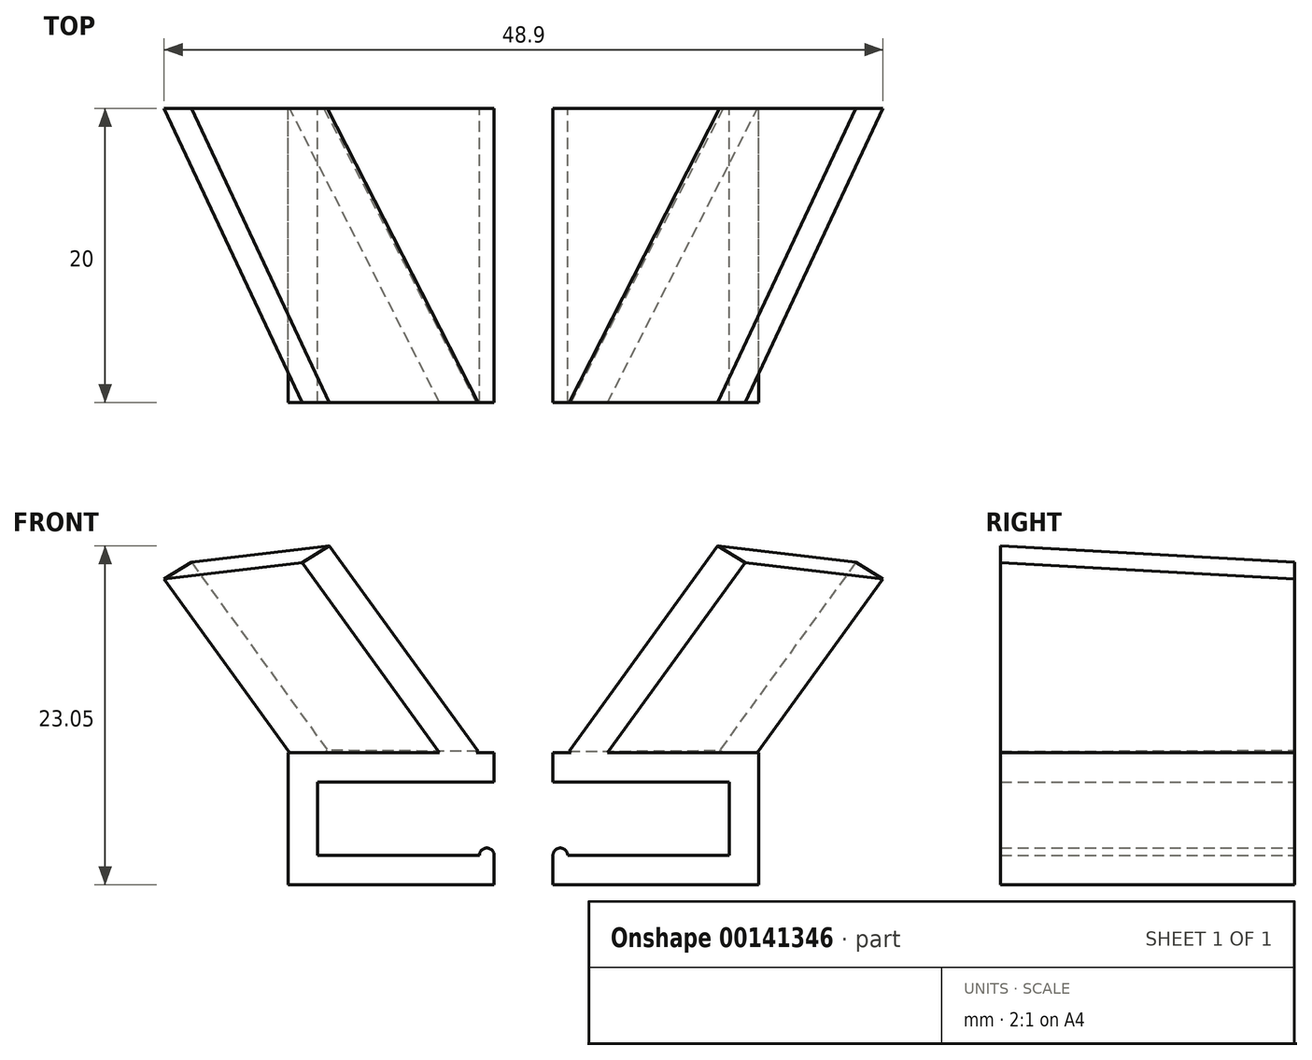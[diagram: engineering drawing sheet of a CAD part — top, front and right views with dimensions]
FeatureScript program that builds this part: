
annotation { "Feature Type Name" : "Feature", "Feature Type Description" : "" }
export const myFeature = defineFeature(function(context is Context, id is Id, definition is map)
    precondition{}
    {
        {
            var Q0;
            Q0=qCreatedBy(makeId("Front.planeOp"),FACE);
            var sketch = newSketch(context, id + "F0", { "sketchPlane" : qUnion([Q0])});
            skLineSegment(sketch, "E0", {"start": v(0, 0) * mm, "end": v(-14, 0) * mm});
            skLineSegment(sketch, "E1", {"start": v(0, 0) * mm, "end": v(0, 9) * mm});
            skLineSegment(sketch, "E2", {"start": v(0, 9) * mm, "end": v(-14, 9) * mm});
            skLineSegment(sketch, "E3", {"start": v(-14, 9) * mm, "end": v(-14, 7) * mm});
            skLineSegment(sketch, "E4", {"start": v(-14, 7) * mm, "end": v(-2, 7) * mm});
            skLineSegment(sketch, "E5", {"start": v(-2, 7) * mm, "end": v(-2, 2) * mm});
            skLineSegment(sketch, "E6", {"start": v(-2, 2) * mm, "end": v(-14, 2) * mm});
            skLineSegment(sketch, "E7", {"start": v(-14, 2) * mm, "end": v(-14, 0) * mm});
            skArc(sketch, "E8", {"start": v(-13, 2) * mm, "mid": v(-13.5, 2.5) * mm, "end": v(-14, 2) * mm});
            skSolve(sketch);
        }
        {
            var Q0;
            Q0=makeQuery(id+"F0.imprint","IMPRINT",FACE,{"disambiguationData":[TD([[makeQuery(id+"F0.imprint","IMPRINT",EDGE,{"derivedFrom":sQuery(id+"F0.wireOp",EDGE,"E0")}),-1.0]])]});
            var Q1;
            {var subQ0=sQuery(id+"F0.wireOp",EDGE,"E8");Q1=makeQuery(id+"F0.imprint","IMPRINT",FACE,{"disambiguationData":[TD([[makeQuery(id+"F0.imprint","IMPRINT",EDGE,{"derivedFrom":subQ0}),1.0]])]});}
            extrude(context, id + "F1", {"entities" : qUnion([Q0, Q1]), "depth" : 20 * mm, "offsetDistance" : 25 * mm});
        }
        {
            var Q0;
            Q0=makeQuery(id+"F1.opExtrude","SWEPT_FACE",FACE,{"disambiguationData":[OSD([sQuery(id+"F0.wireOp",EDGE,"E2")])]});
            var sketch = newSketch(context, id + "F2", { "sketchPlane" : qUnion([Q0])});
            skLineSegment(sketch, "E9", {"start": v(-14.52, -22.87) * mm, "end": v(-2.77, 0) * mm, "construction": true});
            skSolve(sketch);
        }
        {
            var Q0;
            Q0=makeQuery(id+"F1.opExtrude","CAP_FACE",FACE,{"disambiguationData":[OSD([sQuery(id+"F0.wireOp",EDGE,"E0"),sQuery(id+"F0.wireOp",EDGE,"E1"),sQuery(id+"F0.wireOp",EDGE,"E2"),sQuery(id+"F0.wireOp",EDGE,"E3"),sQuery(id+"F0.wireOp",EDGE,"E4"),sQuery(id+"F0.wireOp",EDGE,"E5"),sQuery(id+"F0.wireOp",EDGE,"E6"),sQuery(id+"F0.wireOp",EDGE,"E7"),sQuery(id+"F0.wireOp",EDGE,"E8")])],"isStart":false});
            var sketch = newSketch(context, id + "F3", { "sketchPlane" : qUnion([Q0])});
            skLineSegment(sketch, "E10", {"start": v(-12.96, 9) * mm, "end": v(-1.24, 25.19) * mm, "construction": true});
            skSolve(sketch);
        }
        {
            var Q0;
            Q0=sQuery(id+"F3.wireOp",VERTEX,"E10.end");
            var Q1;
            Q1=sQuery(id+"F3.wireOp",VERTEX,"E10.start");
            var Q2;
            Q2=sQuery(id+"F2.wireOp",VERTEX,"E9.end");
            cPlane(context, id + "F4", {"entities" : qUnion([Q0, Q1, Q2]), "cplaneType" : CPlaneType.THREE_POINT, "offset" : 25 * mm, "width" : 150 * mm, "height" : 150 * mm});
        }
        {
            var Q0;
            Q0=qCreatedBy(id+"F4.planeOp",FACE);
            var sketch = newSketch(context, id + "F5", { "sketchPlane" : qUnion([Q0])});
            skLineSegment(sketch, "E11", {"start": v(27.79, -1.14) * mm, "end": v(-1, 6.93) * mm});
            skLineSegment(sketch, "E12", {"start": v(-1, 6.93) * mm, "end": v(-1, 22.45) * mm});
            skLineSegment(sketch, "E13", {"start": v(-1, 22.45) * mm, "end": v(30.56, 15.75) * mm});
            skLineSegment(sketch, "E14", {"start": v(30.56, 15.75) * mm, "end": v(27.79, -1.14) * mm});
            skSolve(sketch);
        }
        {
            var Q0;
            Q0=makeQuery(id+"F5.imprint","IMPRINT",FACE,{"disambiguationData":[TD([[makeQuery(id+"F5.imprint","IMPRINT",EDGE,{"derivedFrom":sQuery(id+"F5.wireOp",EDGE,"E11")}),-1.0]])]});
            extrude(context, id + "F6", {"entities" : qUnion([Q0]), "operationType" : NewBodyOperationType.ADD, "oppositeDirection" : true, "depth" : 2 * mm, "offsetDistance" : 25 * mm});
        }
        {
            var Q0;
            Q0=makeQuery(id+"F3.imprint","IMPRINT",FACE,{"disambiguationData":[TD([[makeQuery(id+"F3.imprint","IMPRINT",EDGE,{"derivedFrom":makeQuery(id+"F1.opExtrude","CAP_EDGE",EDGE,{"disambiguationData":[OSD([sQuery(id+"F0.wireOp",EDGE,"E0")])],"isStart":false})}),-1.0]])]});
            var sketch = newSketch(context, id + "F7", { "sketchPlane" : qUnion([Q0])});
            skLineSegment(sketch, "E15.bottom", {"start": v(0, 9.84) * mm, "end": v(-15.27, 9.84) * mm});
            skLineSegment(sketch, "E15.top", {"start": v(0, 6.78) * mm, "end": v(-15.27, 6.78) * mm});
            skLineSegment(sketch, "E15.left", {"start": v(0, 9.84) * mm, "end": v(0, 6.78) * mm});
            skLineSegment(sketch, "E15.right", {"start": v(-15.27, 9.84) * mm, "end": v(-15.27, 6.78) * mm});
            skSolve(sketch);
        }
        {
            var Q0;
            {var subQ2=sQuery(id+"F7.wireOp",EDGE,"E15.bottom");Q0=makeQuery(id+"F7.imprint","IMPRINT",FACE,{"disambiguationData":[TD([[makeQuery(id+"F7.imprint","IMPRINT",EDGE,{"derivedFrom":subQ2}),1.0]])]});}
            var Q1;
            {var subQ0=makeQuery(id+"F3.imprint","IMPRINT",EDGE,{"derivedFrom":makeQuery(id+"F1.opExtrude","CAP_EDGE",EDGE,{"disambiguationData":[OSD([sQuery(id+"F0.wireOp",EDGE,"E2")])],"isStart":false})});Q1=makeQuery(id+"F7.imprint","IMPRINT",FACE,{"disambiguationData":[TD([[makeQuery(id+"F7.imprint","IMPRINT",EDGE,{"derivedFrom":subQ0}),1.0]])]});}
            extrude(context, id + "F8", {"entities" : qUnion([Q0, Q1]), "operationType" : NewBodyOperationType.ADD, "depth" : 25 * mm, "offsetDistance" : 25 * mm});
        }
        {
            var Q0;
            Q0=makeQuery(id+"F8.opExtrude","SWEPT_FACE",FACE,{"disambiguationData":[OSD([sQuery(id+"F7.wireOp",EDGE,"E15.top")])]});
            extrude(context, id + "F9", {"entities" : qUnion([Q0]), "operationType" : NewBodyOperationType.REMOVE, "oppositeDirection" : true, "depth" : 25 * mm, "offsetDistance" : 25 * mm});
        }
        {
            var Q0;
            Q0=makeQuery(id+"F1.opExtrude","CAP_FACE",FACE,{"disambiguationData":[OSD([sQuery(id+"F0.wireOp",EDGE,"E0"),sQuery(id+"F0.wireOp",EDGE,"E1"),sQuery(id+"F0.wireOp",EDGE,"E2"),sQuery(id+"F0.wireOp",EDGE,"E3"),sQuery(id+"F0.wireOp",EDGE,"E4"),sQuery(id+"F0.wireOp",EDGE,"E5"),sQuery(id+"F0.wireOp",EDGE,"E6"),sQuery(id+"F0.wireOp",EDGE,"E7"),sQuery(id+"F0.wireOp",EDGE,"E8")])],"isStart":true});
            var sketch = newSketch(context, id + "F10", { "sketchPlane" : qUnion([Q0])});
            skLineSegment(sketch, "E16.bottom", {"start": v(7.12, 8.1) * mm, "end": v(-12.96, 8.1) * mm});
            skLineSegment(sketch, "E16.top", {"start": v(7.12, 1.98) * mm, "end": v(-12.96, 1.98) * mm});
            skLineSegment(sketch, "E16.left", {"start": v(7.12, 8.1) * mm, "end": v(7.12, 1.98) * mm});
            skLineSegment(sketch, "E16.right", {"start": v(-12.96, 8.1) * mm, "end": v(-12.96, 1.98) * mm});
            skSolve(sketch);
        }
        {
            var Q0;
            {var subQ2=sQuery(id+"F0.wireOp",EDGE,"E5");var subQ14=makeQuery(id+"F1.opExtrude","CAP_EDGE",EDGE,{"disambiguationData":[OSD([subQ2])],"isStart":true});Q0=makeQuery(id+"F10.imprint","IMPRINT",FACE,{"disambiguationData":[TD([[makeQuery(id+"F10.imprint","IMPRINT",EDGE,{"derivedFrom":subQ14}),-1.0]])]});}
            var Q1;
            {var subQ0=sQuery(id+"F10.wireOp",EDGE,"E16.right");Q1=makeQuery(id+"F10.imprint","IMPRINT",FACE,{"disambiguationData":[TD([[makeQuery(id+"F10.imprint","IMPRINT",EDGE,{"derivedFrom":subQ0}),1.0]])]});}
            extrude(context, id + "F11", {"entities" : qUnion([Q0, Q1]), "operationType" : NewBodyOperationType.ADD, "depth" : 25 * mm, "offsetDistance" : 25 * mm});
        }
        {
            var Q0;
            Q0=makeQuery(id+"F11.opExtrude","SWEPT_FACE",FACE,{"disambiguationData":[OSD([sQuery(id+"F10.wireOp",EDGE,"E16.top")])]});
            extrude(context, id + "F12", {"entities" : qUnion([Q0]), "operationType" : NewBodyOperationType.REMOVE, "oppositeDirection" : true, "depth" : 25 * mm, "offsetDistance" : 25 * mm});
        }
        {
            var Q0;
            Q0=makeQuery(id+"F1.opExtrude","SWEPT_FACE",FACE,{"disambiguationData":[OSD([sQuery(id+"F0.wireOp",EDGE,"E3")])]});
            cPlane(context, id + "F13", {"entities" : qUnion([Q0]), "cplaneType" : CPlaneType.OFFSET, "offset" : 2 * mm, "width" : 150 * mm, "height" : 150 * mm});
        }
        {
            var Q0;
            Q0=makeQuery(id+"F1.opExtrude","SWEPT_BODY",BODY,{"disambiguationData":[OSD([sQuery(id+"F0.wireOp",EDGE,"E0"),sQuery(id+"F0.wireOp",EDGE,"E1"),sQuery(id+"F0.wireOp",EDGE,"E2"),sQuery(id+"F0.wireOp",EDGE,"E3"),sQuery(id+"F0.wireOp",EDGE,"E4"),sQuery(id+"F0.wireOp",EDGE,"E5"),sQuery(id+"F0.wireOp",EDGE,"E6"),sQuery(id+"F0.wireOp",EDGE,"E7"),sQuery(id+"F0.wireOp",EDGE,"E8")])]});
            var Q1;
            Q1=qCreatedBy(id+"F13.planeOp",FACE);
            mirror(context, id + "F14", {"entities" : qUnion([Q0]), "mirrorPlane" : qUnion([Q1])});
        }
    });
